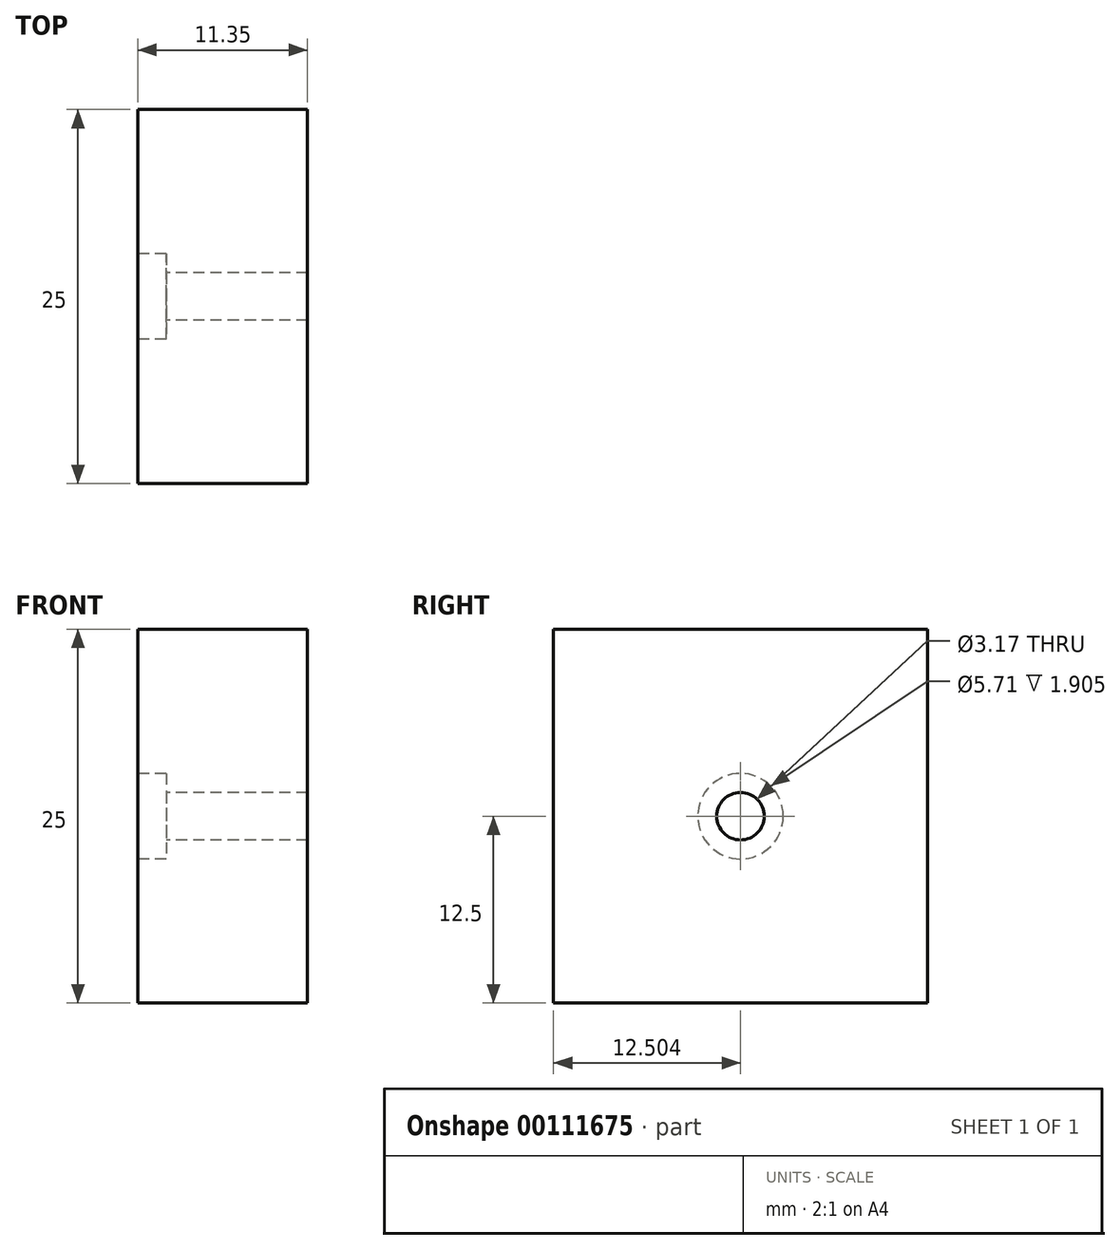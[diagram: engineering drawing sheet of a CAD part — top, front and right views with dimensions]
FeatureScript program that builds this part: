
annotation { "Feature Type Name" : "Feature", "Feature Type Description" : "" }
export const myFeature = defineFeature(function(context is Context, id is Id, definition is map)
    precondition{}
    {
        {
            var Q0;
            Q0=qCreatedBy(makeId("Right.planeOp"),FACE);
            var sketch = newSketch(context, id + "F0", { "sketchPlane" : qUnion([Q0])});
            skLineSegment(sketch, "E0.bottom", {"start": v(-40, 25) * mm, "end": v(-15, 25) * mm});
            skLineSegment(sketch, "E0.top", {"start": v(-40, 0) * mm, "end": v(-15, 0) * mm});
            skLineSegment(sketch, "E0.left", {"start": v(-40, 25) * mm, "end": v(-40, 0) * mm});
            skLineSegment(sketch, "E0.right", {"start": v(-15, 25) * mm, "end": v(-15, 0) * mm});
            skLineSegment(sketch, "E1.bottom", {"start": v(-40, 0) * mm, "end": v(-26.85, 0) * mm});
            skLineSegment(sketch, "E1.top", {"start": v(-40, -6) * mm, "end": v(-26.85, -6) * mm});
            skLineSegment(sketch, "E1.left", {"start": v(-40, 0) * mm, "end": v(-40, -6) * mm});
            skLineSegment(sketch, "E1.right", {"start": v(-26.85, 0) * mm, "end": v(-26.85, -6) * mm});
            skSolve(sketch);
        }
        {
            var Q0;
            Q0=makeQuery(id+"F0.imprint","IMPRINT",FACE,{"disambiguationData":[TD([[makeQuery(id+"F0.imprint","IMPRINT",EDGE,{"derivedFrom":sQuery(id+"F0.wireOp",EDGE,"E1.bottom")}),-1.0]])]});
            var Q1;
            Q1=makeQuery(id+"F0.imprint","IMPRINT",FACE,{"disambiguationData":[TD([[makeQuery(id+"F0.imprint","IMPRINT",EDGE,{"derivedFrom":sQuery(id+"F0.wireOp",EDGE,"E0.bottom")}),-1.0]])]});
            extrude(context, id + "F1", {"entities" : qUnion([Q0, Q1]), "depth" : 5 * mm});
        }
        {
            var Q0;
            Q0=makeQuery(id+"F1.opExtrude","CAP_FACE",FACE,{"disambiguationData":[OSD([sQuery(id+"F0.wireOp",EDGE,"E0.bottom"),sQuery(id+"F0.wireOp",EDGE,"E0.top"),sQuery(id+"F0.wireOp",EDGE,"E0.left"),sQuery(id+"F0.wireOp",EDGE,"E0.right"),sQuery(id+"F0.wireOp",EDGE,"E1.top"),sQuery(id+"F0.wireOp",EDGE,"E1.left"),sQuery(id+"F0.wireOp",EDGE,"E1.right")])],"isStart":true});
            var sketch = newSketch(context, id + "F2", { "sketchPlane" : qUnion([Q0])});
            skLineSegment(sketch, "E2.bottom", {"start": v(15, 25) * mm, "end": v(40, 25) * mm});
            skLineSegment(sketch, "E2.top", {"start": v(15, 0) * mm, "end": v(40, 0) * mm});
            skLineSegment(sketch, "E2.left", {"start": v(15, 25) * mm, "end": v(15, 0) * mm});
            skLineSegment(sketch, "E2.right", {"start": v(40, 25) * mm, "end": v(40, 0) * mm});
            skPoint(sketch, "E2.middle", {"position": v(27.5, 12.5) * mm});
            skSolve(sketch);
        }
        {
            var Q0;
            Q0=sQuery(id+"F2.wireOp",VERTEX,"E2.middle");
            var Q1;
            Q1=makeQuery(id+"F1.opExtrude","SWEPT_BODY",BODY,{"disambiguationData":[OSD([sQuery(id+"F0.wireOp",EDGE,"E0.bottom"),sQuery(id+"F0.wireOp",EDGE,"E0.top"),sQuery(id+"F0.wireOp",EDGE,"E0.left"),sQuery(id+"F0.wireOp",EDGE,"E0.right"),sQuery(id+"F0.wireOp",EDGE,"E1.top"),sQuery(id+"F0.wireOp",EDGE,"E1.left"),sQuery(id+"F0.wireOp",EDGE,"E1.right")])]});
            hole(context, id + "F3", {"style" : HoleStyle.C_BORE, "endStyle" : HoleEndStyle.THROUGH, "holeDiameter" : 3.17 * mm, "cBoreDiameter" : 5.7 * mm, "cBoreDepth" : 1.9 * mm, "locations" : qUnion([Q0]), "scope" : qUnion([Q1]), "isTappedThrough" : true});
        }
        {
            var Q0;
            Q0=makeQuery(id+"F1.opExtrude","CAP_FACE",FACE,{"disambiguationData":[OSD([sQuery(id+"F0.wireOp",EDGE,"E0.bottom"),sQuery(id+"F0.wireOp",EDGE,"E0.top"),sQuery(id+"F0.wireOp",EDGE,"E0.left"),sQuery(id+"F0.wireOp",EDGE,"E0.right"),sQuery(id+"F0.wireOp",EDGE,"E1.top"),sQuery(id+"F0.wireOp",EDGE,"E1.left"),sQuery(id+"F0.wireOp",EDGE,"E1.right")])],"isStart":false});
            var sketch = newSketch(context, id + "F4", { "sketchPlane" : qUnion([Q0])});
            skLineSegment(sketch, "E3", {"start": v(-26.85, 0) * mm, "end": v(-40, 0) * mm});
            skSolve(sketch);
        }
        {
            var Q0;
            {var subQ0=sQuery(id+"F4.wireOp",EDGE,"E3");Q0=makeQuery(id+"F4.imprint","IMPRINT",FACE,{"disambiguationData":[TD([[makeQuery(id+"F4.imprint","IMPRINT",EDGE,{"derivedFrom":subQ0}),1.0]])]});}
            extrude(context, id + "F5", {"entities" : qUnion([Q0]), "operationType" : NewBodyOperationType.ADD, "depth" : 6.35 * mm});
        }
    });
